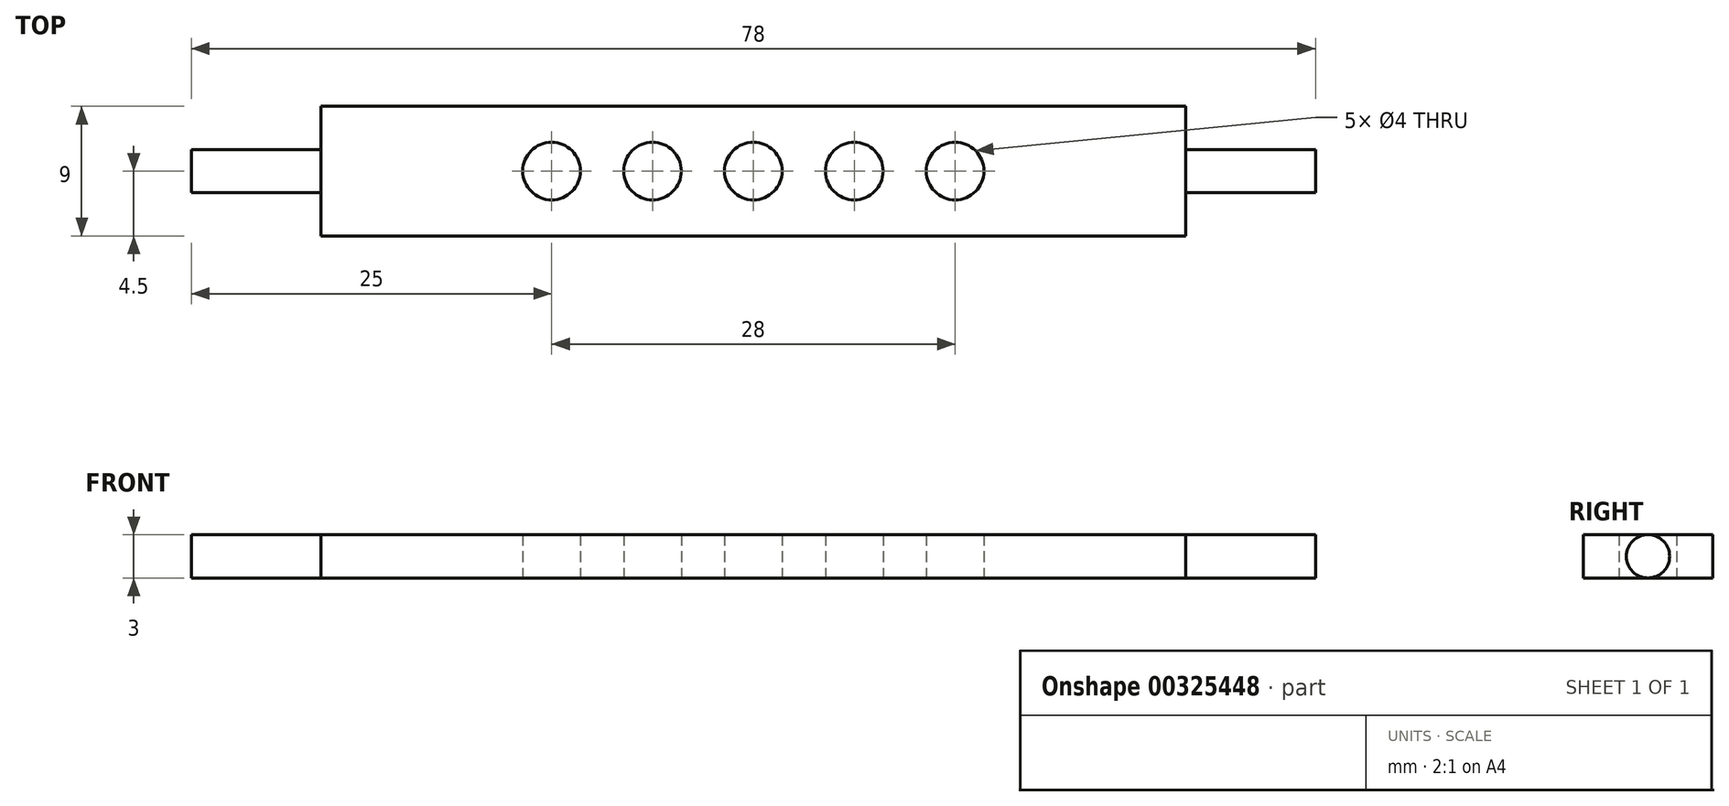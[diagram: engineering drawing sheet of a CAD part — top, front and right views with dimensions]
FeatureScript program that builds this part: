
annotation { "Feature Type Name" : "Feature", "Feature Type Description" : "" }
export const myFeature = defineFeature(function(context is Context, id is Id, definition is map)
    precondition{}
    {
        {
            var Q0;
            Q0=qCreatedBy(makeId("Top.planeOp"),FACE);
            var sketch = newSketch(context, id + "F0", { "sketchPlane" : qUnion([Q0])});
            skLineSegment(sketch, "E0.bottom", {"start": v(30, 4.5) * mm, "end": v(-30, 4.5) * mm});
            skLineSegment(sketch, "E0.top", {"start": v(30, -4.5) * mm, "end": v(-30, -4.5) * mm});
            skLineSegment(sketch, "E0.left", {"start": v(30, 4.5) * mm, "end": v(30, -4.5) * mm});
            skLineSegment(sketch, "E0.right", {"start": v(-30, 4.5) * mm, "end": v(-30, -4.5) * mm});
            skPoint(sketch, "E0.middle", {"position": v(0, 0) * mm});
            skCircle(sketch, "E1", {"center": v(0, 0) * mm, "radius": 2 * mm});
            skCircle(sketch, "E2", {"center": v(7, 0) * mm, "radius": 2 * mm});
            skCircle(sketch, "E3", {"center": v(14, 0) * mm, "radius": 2 * mm});
            skCircle(sketch, "E4.MirrorC", {"center": v(-7, 0) * mm, "radius": 2 * mm});
            skCircle(sketch, "E5.MirrorC", {"center": v(-14, 0) * mm, "radius": 2 * mm});
            skSolve(sketch);
        }
        {
            var Q0;
            Q0=makeQuery(id+"F0.imprint","IMPRINT",FACE,{"disambiguationData":[TD([[makeQuery(id+"F0.imprint","IMPRINT",EDGE,{"derivedFrom":sQuery(id+"F0.wireOp",EDGE,"E0.bottom")}),1.0]])]});
            extrude(context, id + "F1", {"entities" : qUnion([Q0]), "depth" : 3 * mm});
        }
        {
            var Q0;
            Q0=makeQuery(id+"F1.opExtrude","SWEPT_FACE",FACE,{"disambiguationData":[OSD([sQuery(id+"F0.wireOp",EDGE,"E0.right")])]});
            var sketch = newSketch(context, id + "F2", { "sketchPlane" : qUnion([Q0])});
            skCircle(sketch, "E6", {"center": v(0, 1.5) * mm, "radius": 1.5 * mm});
            skPoint(sketch, "E6.centerSnap0", {"position": v(-4.5, 1.5) * mm});
            skSolve(sketch);
        }
        {
            var Q0;
            {var subQ0=sQuery(id+"F2.wireOp",EDGE,"E6");var subQ1=sQuery(id+"F0.wireOp",EDGE,"E0.right");var subQ2=makeQuery(id+"F2.imprint","INTERSECT",VERTEX,{"derivedFrom":[makeQuery(id+"F1.opExtrude","CAP_EDGE",EDGE,{"disambiguationData":[OSD([subQ1])],"isStart":true}),subQ0]});Q0=makeQuery(id+"F2.imprint","IMPRINT",FACE,{"disambiguationData":[TD([[makeQuery(id+"F2.imprint","IMPRINT",EDGE,{"disambiguationData":[TD([[subQ2,1.0]])],"derivedFrom":subQ0}),1.0]])]});}
            extrude(context, id + "F3", {"entities" : qUnion([Q0]), "operationType" : NewBodyOperationType.ADD, "depth" : 9 * mm});
        }
        {
            var Q0;
            Q0=makeQuery(id+"F1.opExtrude","SWEPT_FACE",FACE,{"disambiguationData":[OSD([sQuery(id+"F0.wireOp",EDGE,"E0.left")])]});
            var sketch = newSketch(context, id + "F4", { "sketchPlane" : qUnion([Q0])});
            skCircle(sketch, "E7", {"center": v(0, 1.5) * mm, "radius": 1.5 * mm});
            skPoint(sketch, "E7.centerSnap0", {"position": v(4.5, 1.5) * mm});
            skSolve(sketch);
        }
        {
            var Q0;
            {var subQ0=sQuery(id+"F4.wireOp",EDGE,"E7");var subQ1=sQuery(id+"F0.wireOp",EDGE,"E0.left");var subQ2=makeQuery(id+"F4.imprint","INTERSECT",VERTEX,{"derivedFrom":[makeQuery(id+"F1.opExtrude","CAP_EDGE",EDGE,{"disambiguationData":[OSD([subQ1])],"isStart":true}),subQ0]});Q0=makeQuery(id+"F4.imprint","IMPRINT",FACE,{"disambiguationData":[TD([[makeQuery(id+"F4.imprint","IMPRINT",EDGE,{"disambiguationData":[TD([[subQ2,1.0]])],"derivedFrom":subQ0}),1.0]])]});}
            extrude(context, id + "F5", {"entities" : qUnion([Q0]), "operationType" : NewBodyOperationType.ADD, "depth" : 9 * mm});
        }
    });
